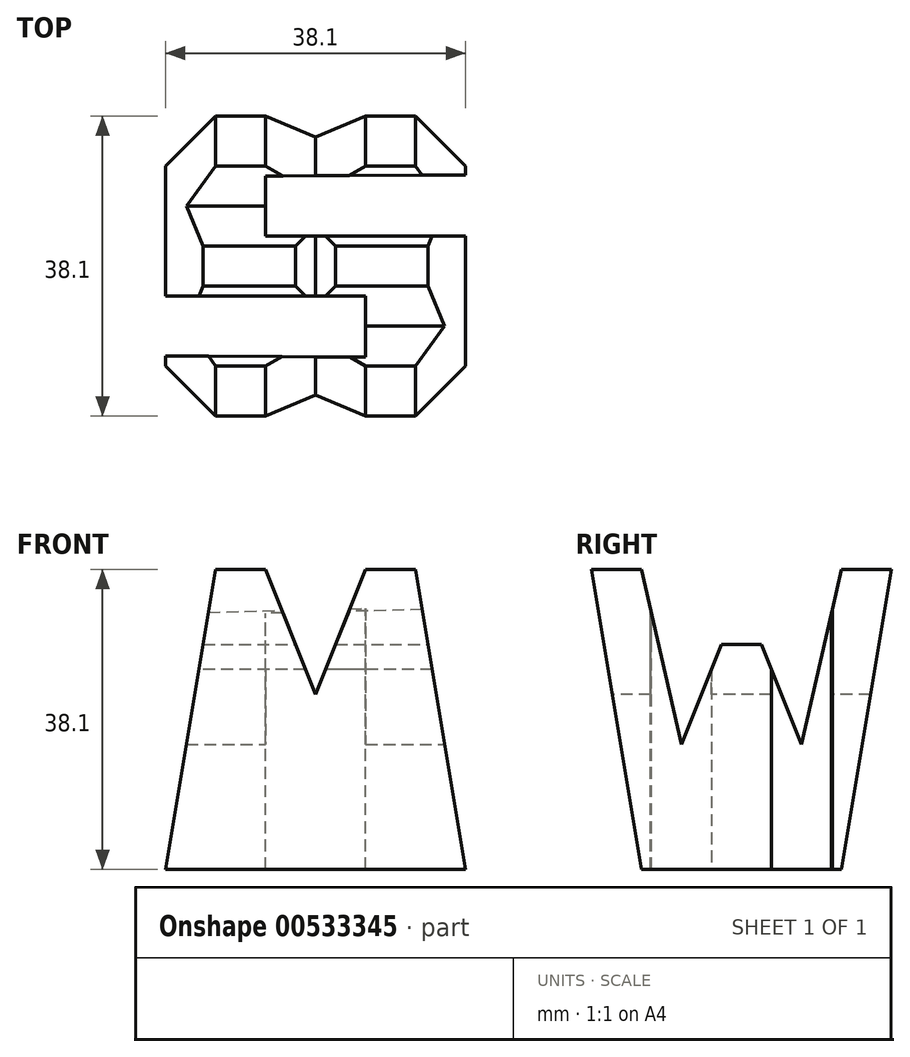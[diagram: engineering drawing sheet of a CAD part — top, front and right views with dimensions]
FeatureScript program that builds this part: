
annotation { "Feature Type Name" : "Feature", "Feature Type Description" : "" }
export const myFeature = defineFeature(function(context is Context, id is Id, definition is map)
    precondition{}
    {
        {
            var Q0;
            Q0=qCreatedBy(makeId("Front.planeOp"),FACE);
            var sketch = newSketch(context, id + "F0", { "sketchPlane" : qUnion([Q0])});
            skLineSegment(sketch, "E0", {"start": v(0, 0) * mm, "end": v(0, 38.1) * mm});
            skLineSegment(sketch, "E1", {"start": v(0, 38.1) * mm, "end": v(38.1, 38.1) * mm});
            skLineSegment(sketch, "E2", {"start": v(38.1, 38.1) * mm, "end": v(38.1, 0) * mm});
            skLineSegment(sketch, "E3", {"start": v(38.1, 0) * mm, "end": v(0, 0) * mm});
            skSolve(sketch);
        }
        {
            var Q0;
            Q0 = qSketchRegion(id + "F0", true);
            extrude(context, id + "F1", {"entities" : qUnion([Q0]), "depth" : 38.1 * mm, "offsetDistance" : 25.4 * mm});
        }
        {
            var Q0;
            Q0=qCreatedBy(makeId("Front.planeOp"),FACE);
            cPlane(context, id + "F2", {"entities" : qUnion([Q0]), "cplaneType" : CPlaneType.OFFSET, "offset" : 38.1 * mm, "width" : 152.4 * mm, "height" : 152.4 * mm});
        }
        {
            var Q0;
            Q0=qCreatedBy(makeId("Right.planeOp"),FACE);
            cPlane(context, id + "F3", {"entities" : qUnion([Q0]), "cplaneType" : CPlaneType.OFFSET, "offset" : 38.1 * mm, "width" : 152.4 * mm, "height" : 152.4 * mm});
        }
        {
            var Q0;
            Q0=qCreatedBy(makeId("Top.planeOp"),FACE);
            cPlane(context, id + "F4", {"entities" : qUnion([Q0]), "cplaneType" : CPlaneType.OFFSET, "offset" : 38.1 * mm, "width" : 152.4 * mm, "height" : 152.4 * mm});
        }
        {
            var Q0;
            Q0=qCreatedBy(id+"F3.planeOp",FACE);
            var sketch = newSketch(context, id + "F5", { "sketchPlane" : qUnion([Q0])});
            skLineSegment(sketch, "E4", {"start": v(0, 0) * mm, "end": v(0, 38.1) * mm});
            skLineSegment(sketch, "E5", {"start": v(-38.1, 38.1) * mm, "end": v(-38.1, 0) * mm});
            skLineSegment(sketch, "E6", {"start": v(-38.1, 0) * mm, "end": v(0, 0) * mm});
            skLineSegment(sketch, "E7", {"start": v(-38.1, 38.1) * mm, "end": v(-31.75, 0) * mm});
            skLineSegment(sketch, "E8", {"start": v(-31.75, 38.1) * mm, "end": v(-26.67, 15.87) * mm});
            skLineSegment(sketch, "E9", {"start": v(-26.67, 15.87) * mm, "end": v(-21.59, 28.57) * mm});
            skLineSegment(sketch, "E10", {"start": v(-21.59, 28.57) * mm, "end": v(-16.51, 28.57) * mm});
            skLineSegment(sketch, "E11", {"start": v(-16.5, 28.57) * mm, "end": v(-11.43, 15.87) * mm});
            skLineSegment(sketch, "E12", {"start": v(-11.43, 15.87) * mm, "end": v(-6.35, 38.1) * mm});
            skLineSegment(sketch, "E13", {"start": v(-6.35, 38.1) * mm, "end": v(0, 38.1) * mm});
            skLineSegment(sketch, "E14", {"start": v(0, 38.1) * mm, "end": v(-6.35, 0) * mm});
            skLineSegment(sketch, "E15", {"start": v(-19.05, 15.87) * mm, "end": v(-12.7, 0) * mm});
            skLineSegment(sketch, "E16", {"start": v(-12.7, 0) * mm, "end": v(-19.05, 15.87) * mm});
            skLineSegment(sketch, "E17", {"start": v(-19.05, 15.87) * mm, "end": v(-25.4, 0) * mm});
            skLineSegment(sketch, "E18", {"start": v(-38.1, 38.1) * mm, "end": v(-31.75, 38.1) * mm});
            skLineSegment(sketch, "E19", {"start": v(-31.75, 0) * mm, "end": v(-25.4, 0) * mm});
            skLineSegment(sketch, "E20", {"start": v(-12.7, 0) * mm, "end": v(-6.35, 0) * mm});
            skLineSegment(sketch, "E21", {"start": v(-38.1, 38.1) * mm, "end": v(0, 38.1) * mm});
            skSolve(sketch);
        }
        {
            var Q0;
            {var subQ0=sQuery(id+"F5.wireOp",EDGE,"E4");Q0=makeQuery(id+"F5.imprint","IMPRINT",FACE,{"disambiguationData":[TD([[makeQuery(id+"F5.imprint","IMPRINT",EDGE,{"derivedFrom":subQ0}),1.0]])]});}
            var Q1;
            {var subQ0=sQuery(id+"F5.wireOp",EDGE,"E16");Q1=makeQuery(id+"F5.imprint","IMPRINT",FACE,{"disambiguationData":[TD([[makeQuery(id+"F5.imprint","IMPRINT",EDGE,{"derivedFrom":subQ0}),1.0]])]});}
            var Q2;
            {var subQ0=sQuery(id+"F5.wireOp",EDGE,"E5");Q2=makeQuery(id+"F5.imprint","IMPRINT",FACE,{"disambiguationData":[TD([[makeQuery(id+"F5.imprint","IMPRINT",EDGE,{"derivedFrom":subQ0}),1.0]])]});}
            var Q3;
            {var subQ0=sQuery(id+"F5.wireOp",EDGE,"E8");Q3=makeQuery(id+"F5.imprint","IMPRINT",FACE,{"disambiguationData":[TD([[makeQuery(id+"F5.imprint","IMPRINT",EDGE,{"derivedFrom":subQ0}),1.0]])]});}
            extrude(context, id + "F6", {"entities" : qUnion([Q0, Q1, Q2, Q3]), "operationType" : NewBodyOperationType.REMOVE, "oppositeDirection" : true, "depth" : 38.1 * mm, "offsetDistance" : 25.4 * mm});
        }
        {
            var Q0;
            Q0=qCreatedBy(id+"F2.planeOp",FACE);
            var sketch = newSketch(context, id + "F7", { "sketchPlane" : qUnion([Q0])});
            skLineSegment(sketch, "E22", {"start": v(0, 38.1) * mm, "end": v(38.1, 38.1) * mm});
            skLineSegment(sketch, "E23", {"start": v(38.1, 38.1) * mm, "end": v(38.1, 0) * mm});
            skLineSegment(sketch, "E24", {"start": v(38.1, 0) * mm, "end": v(0, 0) * mm});
            skLineSegment(sketch, "E25", {"start": v(0, 0) * mm, "end": v(0, 38.1) * mm});
            skLineSegment(sketch, "E26", {"start": v(6.35, 38.1) * mm, "end": v(12.7, 38.1) * mm});
            skLineSegment(sketch, "E27", {"start": v(12.7, 38.1) * mm, "end": v(19.05, 22.22) * mm});
            skLineSegment(sketch, "E28", {"start": v(19.05, 22.22) * mm, "end": v(25.4, 38.1) * mm});
            skLineSegment(sketch, "E29", {"start": v(31.75, 38.1) * mm, "end": v(38.1, 0) * mm});
            skLineSegment(sketch, "E30", {"start": v(0, 0) * mm, "end": v(6.35, 38.1) * mm});
            skLineSegment(sketch, "E31", {"start": v(11.43, 22.23) * mm, "end": v(6.35, 0) * mm});
            skLineSegment(sketch, "E32", {"start": v(6.35, 0) * mm, "end": v(11.43, 22.23) * mm});
            skLineSegment(sketch, "E33", {"start": v(11.43, 22.23) * mm, "end": v(16.5, 9.52) * mm});
            skLineSegment(sketch, "E34", {"start": v(16.5, 9.52) * mm, "end": v(21.59, 9.52) * mm});
            skLineSegment(sketch, "E35", {"start": v(21.59, 9.52) * mm, "end": v(26.67, 22.23) * mm});
            skLineSegment(sketch, "E36", {"start": v(26.67, 22.23) * mm, "end": v(31.75, 0) * mm});
            skSolve(sketch);
        }
        {
            var Q0;
            {var subQ0=sQuery(id+"F7.wireOp",EDGE,"E27");Q0=makeQuery(id+"F7.imprint","IMPRINT",FACE,{"disambiguationData":[TD([[makeQuery(id+"F7.imprint","IMPRINT",EDGE,{"derivedFrom":subQ0}),1.0]])]});}
            var Q1;
            {var subQ0=sQuery(id+"F7.wireOp",EDGE,"E23");Q1=makeQuery(id+"F7.imprint","IMPRINT",FACE,{"disambiguationData":[TD([[makeQuery(id+"F7.imprint","IMPRINT",EDGE,{"derivedFrom":subQ0}),-1.0]])]});}
            var Q2;
            {var subQ0=sQuery(id+"F7.wireOp",EDGE,"E32");Q2=makeQuery(id+"F7.imprint","IMPRINT",FACE,{"disambiguationData":[TD([[makeQuery(id+"F7.imprint","IMPRINT",EDGE,{"derivedFrom":subQ0}),-1.0]])]});}
            var Q3;
            {var subQ0=sQuery(id+"F7.wireOp",EDGE,"E25");Q3=makeQuery(id+"F7.imprint","IMPRINT",FACE,{"disambiguationData":[TD([[makeQuery(id+"F7.imprint","IMPRINT",EDGE,{"derivedFrom":subQ0}),-1.0]])]});}
            extrude(context, id + "F8", {"entities" : qUnion([Q0, Q1, Q2, Q3]), "operationType" : NewBodyOperationType.REMOVE, "oppositeDirection" : true, "depth" : 38.1 * mm, "offsetDistance" : 25.4 * mm});
        }
        {
            var Q0;
            Q0=qCreatedBy(id+"F4.planeOp",FACE);
            var sketch = newSketch(context, id + "F9", { "sketchPlane" : qUnion([Q0])});
            skLineSegment(sketch, "E37", {"start": v(0, 0) * mm, "end": v(38.1, 0) * mm});
            skLineSegment(sketch, "E38", {"start": v(38.1, 0) * mm, "end": v(38.1, -38.1) * mm});
            skLineSegment(sketch, "E39", {"start": v(38.1, -38.1) * mm, "end": v(0, -38.1) * mm});
            skLineSegment(sketch, "E40", {"start": v(0, -38.1) * mm, "end": v(0, 0) * mm});
            skLineSegment(sketch, "E41", {"start": v(12.7, -7.62) * mm, "end": v(12.7, -15.24) * mm});
            skLineSegment(sketch, "E42", {"start": v(12.7, -15.24) * mm, "end": v(38.1, -15.24) * mm});
            skLineSegment(sketch, "E43", {"start": v(38.1, -15.24) * mm, "end": v(12.7, -15.24) * mm});
            skLineSegment(sketch, "E44", {"start": v(38.1, -7.48) * mm, "end": v(38.8, -7.48) * mm});
            skLineSegment(sketch, "E45", {"start": v(38.8, -7.48) * mm, "end": v(38.8, -15.5) * mm});
            skLineSegment(sketch, "E46", {"start": v(0, -22.86) * mm, "end": v(25.4, -22.86) * mm});
            skLineSegment(sketch, "E47", {"start": v(25.4, -22.86) * mm, "end": v(25.4, -30.62) * mm});
            skLineSegment(sketch, "E48", {"start": v(25.4, -30.62) * mm, "end": v(0, -30.48) * mm});
            skLineSegment(sketch, "E49", {"start": v(12.7, -7.62) * mm, "end": v(38.8, -7.48) * mm});
            skSolve(sketch);
        }
        {
            var Q0;
            {var subQ4=sQuery(id+"F9.wireOp",EDGE,"E41");Q0=makeQuery(id+"F9.imprint","IMPRINT",FACE,{"disambiguationData":[TD([[makeQuery(id+"F9.imprint","IMPRINT",EDGE,{"derivedFrom":subQ4}),1.0]])]});}
            var Q1;
            {var subQ0=sQuery(id+"F9.wireOp",EDGE,"E46");Q1=makeQuery(id+"F9.imprint","IMPRINT",FACE,{"disambiguationData":[TD([[makeQuery(id+"F9.imprint","IMPRINT",EDGE,{"derivedFrom":subQ0}),-1.0]])]});}
            extrude(context, id + "F10", {"entities" : qUnion([Q0, Q1]), "operationType" : NewBodyOperationType.REMOVE, "oppositeDirection" : true, "depth" : 38.1 * mm, "offsetDistance" : 25.4 * mm});
        }
    });
